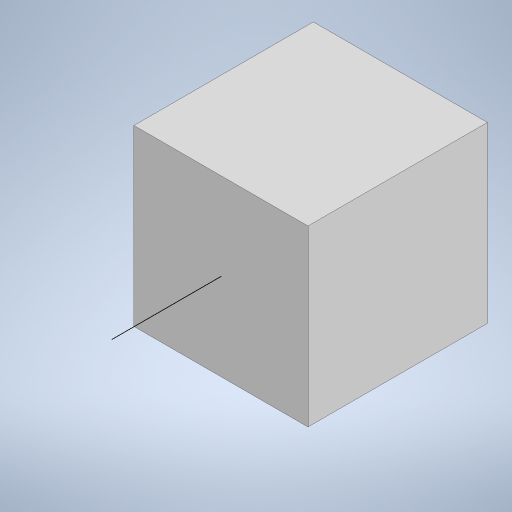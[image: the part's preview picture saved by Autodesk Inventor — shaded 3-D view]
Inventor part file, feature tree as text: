
AUTODESK INVENTOR PART (.ipt)
format: ipt  version: 2023 (Build 270158000, 158)  size: 330,240 bytes
history: native  units: in
note: dims shown in document units (in); Inventor stores cm internally (conversion verified against a paired STEP export)
features: sketch x13, extrude x10, projected_geometry x8, plane x2, other x1
ambient origin geometry x8: Origin, YZ Plane, XZ Plane, XY Plane, X Axis, Y Axis, Z Axis, Center Point
bodies: Solid1 (feature_tree)
feature tree (34):
  extrude  "Extrusion1"  Depth=0.874in
  extrude  "Extrusion2"  Depth=0.315in
  sketch  "Sketch3"  dims[d5=0.2854in d6=0.0in d9=0.2165in]
  extrude  "Extrusion4"  Depth=0.2165in
  extrude  "Extrusion5"  Depth=0.0886in
  extrude  "Extrusion6"  Depth=0.374in
  extrude  "Extrusion8"  Depth=0.0886in TaperAngle=0.0deg
  extrude  "Extrusion9"  Depth=0.2362in TaperAngle=0.0deg
  extrude  "Extrusion10"  Depth=0.1378in TaperAngle=0.0deg
  sketch  "Sketch12"  dims[d41=0.4409in d48=0.3543in]
  plane  "Work Plane2"
  extrude  "Extrusion12"  Depth=0.0394in
  plane  "Work Plane4"
  sketch  "Sketch18"  dims[d50=0.0787in]
  extrude  "Extrusion13"  Depth=0.3543in
  sketch  "Sketch1"  dims[d0=0.874in d1=0.874in]
  sketch  "Sketch2"  dims[d2=0.315in d3=0.0in d4=0.6299in]
  projected_geometry  "Projected Loop1"
  sketch  "Sketch5"  dims[d10=0.0886in d11=0.0in d12=0.2165in]
  projected_geometry  "Projected Loop3"
  sketch  "Sketch6"  dims[d13=0.0886in d14=0.0in d15=0.374in]
  projected_geometry  "Projected Loop4"
  sketch  "Sketch7"  dims[d16=0.0886in d17=0.0in d23=0.0886in d24=0.0in]
  projected_geometry  "Projected Loop5"
  sketch  "Sketch9"  dims[d25=0.0787in d26=0.2362in d27=0.0in]
  projected_geometry  "Projected Loop8"
  sketch  "Sketch10"  dims[d28=0.7307in d29=0.1378in d30=0.0in]
  projected_geometry  "Projected Loop9"
  sketch  "Sketch11"  dims[d31=1.063in d36=0.0394in]
  sketch  "Sketch17"  dims[d49=0.1083in]
  projected_geometry  "Projected Loop11"
  sketch  "Sketch19"  dims[d52=0.1083in d53=0.0787in d54=0.0in d55=0.0in d56=-0.437in d57=0.0787in d58=0.9562in d59=0.0in]
  projected_geometry  "Projected Loop12"
  other  "camera block"
